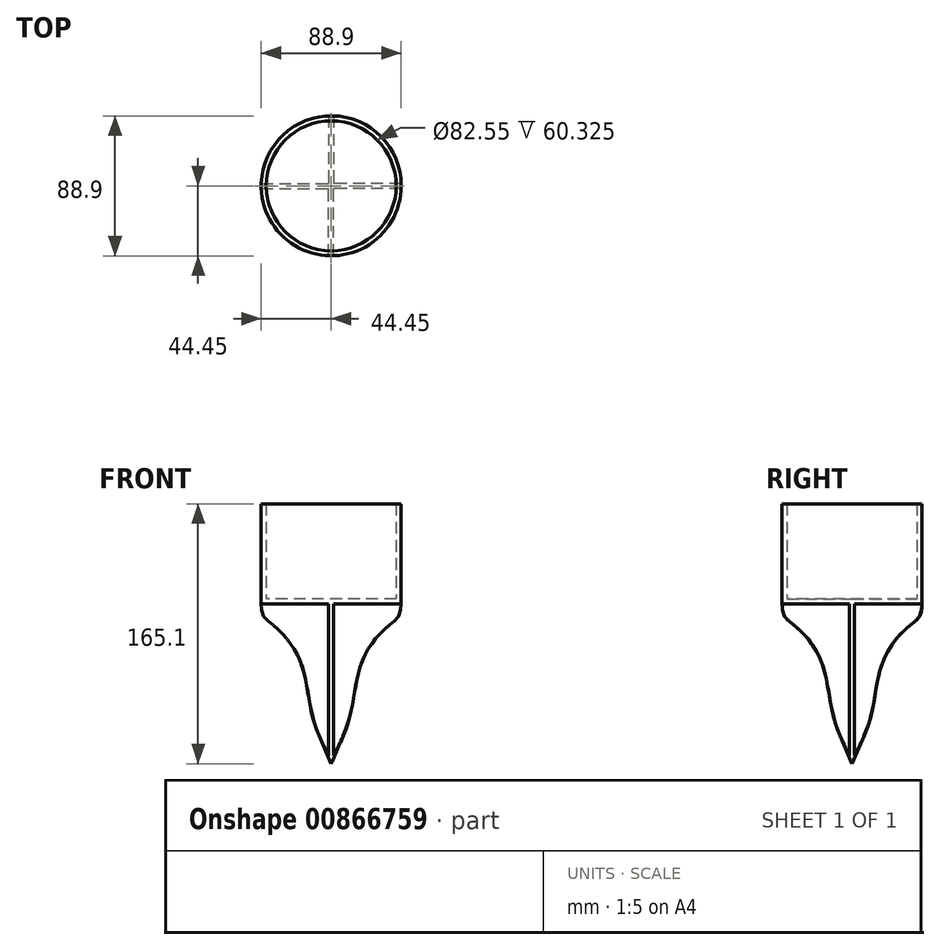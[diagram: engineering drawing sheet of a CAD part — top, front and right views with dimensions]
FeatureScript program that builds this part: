
annotation { "Feature Type Name" : "Feature", "Feature Type Description" : "" }
export const myFeature = defineFeature(function(context is Context, id is Id, definition is map)
    precondition{}
    {
        {
            var Q0;
            Q0=qCreatedBy(makeId("Front.planeOp"),FACE);
            var sketch = newSketch(context, id + "F0", { "sketchPlane" : qUnion([Q0])});
            skLineSegment(sketch, "E0", {"start": v(0, 0) * mm, "end": v(7.8, 17.83) * mm});
            skLineSegment(sketch, "E1", {"start": v(44.45, 101.6) * mm, "end": v(0, 101.6) * mm});
            skLineSegment(sketch, "E2", {"start": v(0, 101.6) * mm, "end": v(0, 0) * mm});
            skFitSpline(sketch, "E3", {"points": [v(7.8, 17.83) * mm, v(19.54, 64.73) * mm, v(37.06, 88.14) * mm, v(44.45, 101.6) * mm], "startDerivative": vector(49.84, 113.96) * mm, "endDerivative": vector(0, 110.88) * mm});
            skSolve(sketch);
        }
        {
            var Q0;
            Q0=makeQuery(id+"F0.imprint","IMPRINT",FACE,{"disambiguationData":[TD([[makeQuery(id+"F0.imprint","IMPRINT",EDGE,{"derivedFrom":sQuery(id+"F0.wireOp",EDGE,"E0")}),1.0]])]});
            var Q1;
            Q1=sQuery(id+"F0.wireOp",EDGE,"E2");
            revolve(context, id + "F1", {"surfaceOperationType" : NewSurfaceOperationType.NEW, "entities" : qUnion([Q0]), "axis" : qUnion([Q1]), "revolveType" : RevolveType.FULL});
        }
        {
            var Q0;
            Q0=qCreatedBy(makeId("Top.planeOp"),FACE);
            var sketch = newSketch(context, id + "F2", { "sketchPlane" : qUnion([Q0])});
            skLineSegment(sketch, "E4.bottom", {"start": v(-1.59, -1.59) * mm, "end": v(-67.09, -1.59) * mm});
            skLineSegment(sketch, "E4.top", {"start": v(-1.59, -67.09) * mm, "end": v(-67.09, -67.09) * mm});
            skLineSegment(sketch, "E4.left", {"start": v(-1.59, -1.59) * mm, "end": v(-1.59, -67.09) * mm});
            skLineSegment(sketch, "E4.right", {"start": v(-67.09, -1.59) * mm, "end": v(-67.09, -67.09) * mm});
            skLineSegment(sketch, "E5.bottom", {"start": v(-1.59, 1.59) * mm, "end": v(-67.09, 1.59) * mm});
            skLineSegment(sketch, "E5.top", {"start": v(-1.59, 69.86) * mm, "end": v(-67.09, 69.86) * mm});
            skLineSegment(sketch, "E5.left", {"start": v(-1.59, 1.59) * mm, "end": v(-1.59, 69.86) * mm});
            skLineSegment(sketch, "E5.right", {"start": v(-67.09, 1.59) * mm, "end": v(-67.09, 69.86) * mm});
            skLineSegment(sketch, "E6.bottom", {"start": v(1.59, 1.59) * mm, "end": v(67.09, 1.59) * mm});
            skLineSegment(sketch, "E6.top", {"start": v(1.59, 69.86) * mm, "end": v(67.09, 69.86) * mm});
            skLineSegment(sketch, "E6.left", {"start": v(1.59, 1.59) * mm, "end": v(1.59, 69.86) * mm});
            skLineSegment(sketch, "E6.right", {"start": v(67.09, 1.59) * mm, "end": v(67.09, 69.86) * mm});
            skLineSegment(sketch, "E7.bottom", {"start": v(1.59, -1.59) * mm, "end": v(67.09, -1.59) * mm});
            skLineSegment(sketch, "E7.top", {"start": v(1.59, -67.09) * mm, "end": v(67.09, -67.09) * mm});
            skLineSegment(sketch, "E7.left", {"start": v(1.59, -1.59) * mm, "end": v(1.59, -67.09) * mm});
            skLineSegment(sketch, "E7.right", {"start": v(67.09, -1.59) * mm, "end": v(67.09, -67.09) * mm});
            skLineSegment(sketch, "E8", {"start": v(-1.59, -1.59) * mm, "end": v(1.59, 1.59) * mm});
            skLineSegment(sketch, "E9", {"start": v(-67.09, -1.59) * mm, "end": v(-67.09, 1.59) * mm, "construction": true});
            skLineSegment(sketch, "E10", {"start": v(-1.59, -67.09) * mm, "end": v(1.59, -67.09) * mm, "construction": true});
            skSolve(sketch);
        }
        {
            var Q0;
            Q0 = qSketchRegion(id + "F2", true);
            var Q1;
            Q1=makeQuery(id+"F1.opRevolve","SWEPT_FACE",FACE,{"disambiguationData":[OSD([sQuery(id+"F0.wireOp",EDGE,"E1")])]});
            extrude(context, id + "F3", {"entities" : qUnion([Q0]), "operationType" : NewBodyOperationType.REMOVE, "endBound" : BoundingType.UP_TO_SURFACE, "depth" : 58.67 * mm, "endBoundEntityFace" : qUnion([Q1]), "offsetDistance" : 25.4 * mm});
        }
        {
            var Q0;
            Q0=makeQuery(id+"F1.opRevolve","SWEPT_FACE",FACE,{"disambiguationData":[OSD([sQuery(id+"F0.wireOp",EDGE,"E1")])]});
            var sketch = newSketch(context, id + "F4", { "sketchPlane" : qUnion([Q0])});
            skCircle(sketch, "E11.0", {"center": v(0, 0) * mm, "radius": 44.45 * mm});
            skSolve(sketch);
        }
        {
            var Q0;
            Q0 = qSketchRegion(id + "F4", true);
            extrude(context, id + "F5", {"entities" : qUnion([Q0]), "operationType" : NewBodyOperationType.ADD, "depth" : 63.5 * mm, "offsetDistance" : 25.4 * mm});
        }
        {
            var Q0;
            Q0=makeQuery(id+"F5.opExtrude","CAP_FACE",FACE,{"disambiguationData":[OSD([sQuery(id+"F4.wireOp",EDGE,"E11.0")])],"isStart":false});
            shell(context, id + "F6", {"entities" : qUnion([Q0]), "thickness" : 3.17 * mm});
        }
    });
